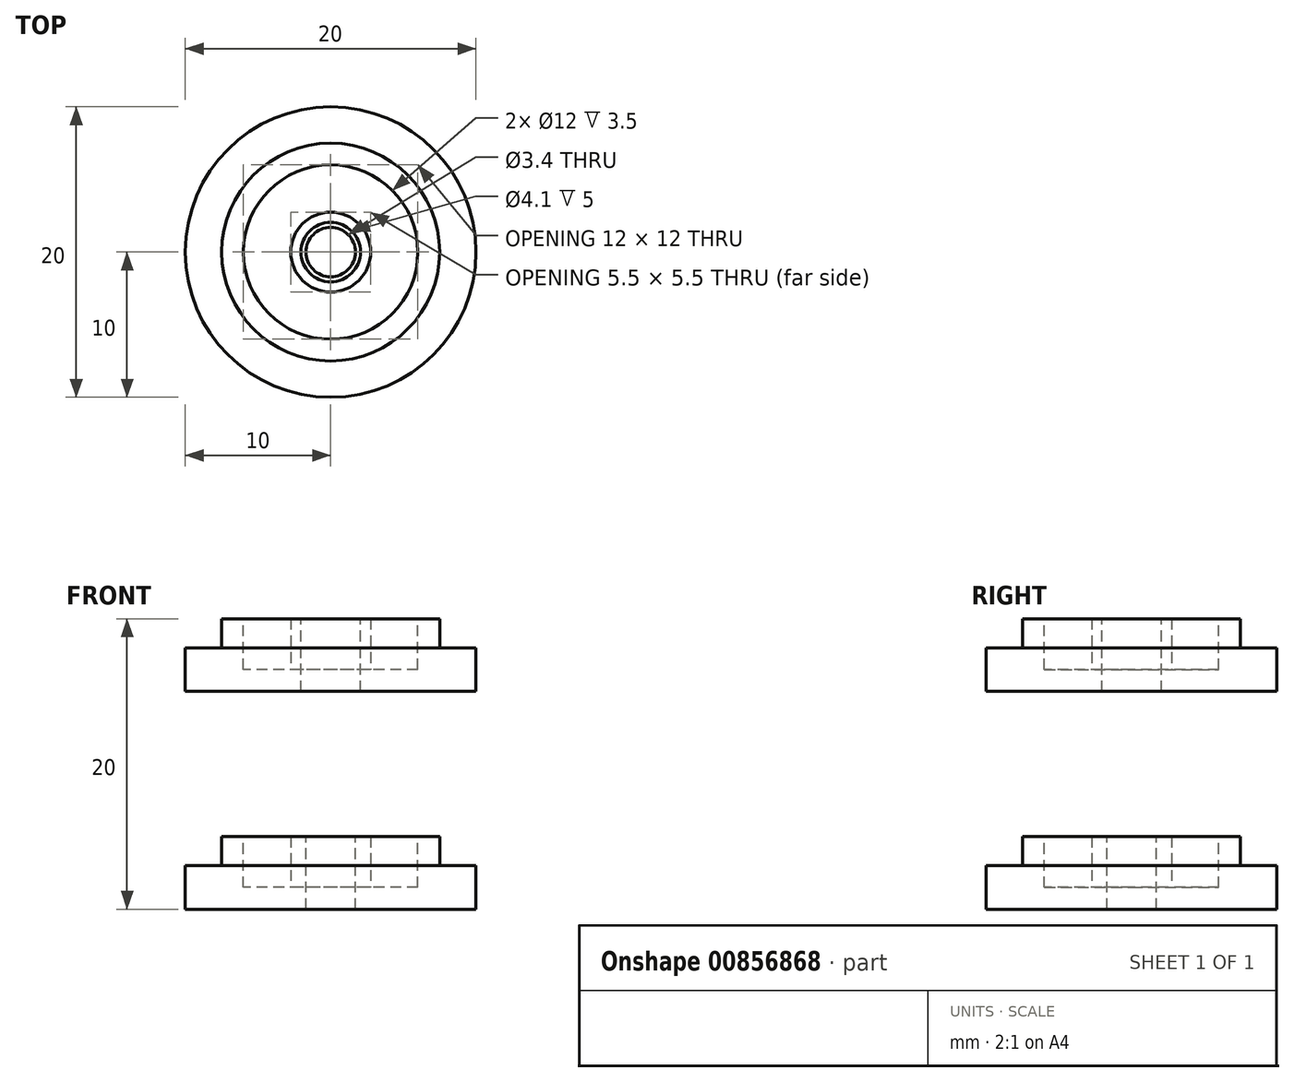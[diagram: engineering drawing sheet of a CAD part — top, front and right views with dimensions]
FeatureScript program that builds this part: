
annotation { "Feature Type Name" : "Feature", "Feature Type Description" : "" }
export const myFeature = defineFeature(function(context is Context, id is Id, definition is map)
    precondition{}
    {
        {
            var Q0;
            Q0=qCreatedBy(makeId("Right.planeOp"),FACE);
            var sketch = newSketch(context, id + "F0", { "sketchPlane" : qUnion([Q0])});
            skLineSegment(sketch, "E0", {"start": v(-7.5, 0) * mm, "end": v(-7.5, 2) * mm});
            skLineSegment(sketch, "E1", {"start": v(-7.5, 2) * mm, "end": v(0, 2) * mm});
            skLineSegment(sketch, "E2", {"start": v(0, 2) * mm, "end": v(0, 0) * mm});
            skLineSegment(sketch, "E3", {"start": v(0, 0) * mm, "end": v(-7.5, 0) * mm});
            skLineSegment(sketch, "E4.bottom", {"start": v(0, 0) * mm, "end": v(-10, 0) * mm});
            skLineSegment(sketch, "E4.top", {"start": v(0, -3) * mm, "end": v(-10, -3) * mm});
            skLineSegment(sketch, "E4.left", {"start": v(0, 0) * mm, "end": v(0, -3) * mm});
            skLineSegment(sketch, "E4.right", {"start": v(-10, 0) * mm, "end": v(-10, -3) * mm});
            skSolve(sketch);
        }
        {
            var Q0;
            Q0=makeQuery(id+"F0.imprint","IMPRINT",FACE,{"disambiguationData":[TD([[makeQuery(id+"F0.imprint","IMPRINT",EDGE,{"derivedFrom":sQuery(id+"F0.wireOp",EDGE,"E0")}),-1.0]])]});
            var Q1;
            Q1=makeQuery(id+"F0.imprint","IMPRINT",FACE,{"disambiguationData":[TD([[makeQuery(id+"F0.imprint","IMPRINT",EDGE,{"derivedFrom":sQuery(id+"F0.wireOp",EDGE,"E3")}),1.0]])]});
            var Q2;
            Q2=sQuery(id+"F0.wireOp",EDGE,"E2");
            revolve(context, id + "F1", {"surfaceOperationType" : NewSurfaceOperationType.NEW, "entities" : qUnion([Q0, Q1]), "axis" : qUnion([Q2]), "revolveType" : RevolveType.FULL});
        }
        {
            var Q0;
            Q0=makeQuery(id+"F1.opRevolve","SWEPT_FACE",FACE,{"disambiguationData":[OSD([sQuery(id+"F0.wireOp",EDGE,"E1")])]});
            shell(context, id + "F2", {"entities" : qUnion([Q0]), "thickness" : 1.5 * mm});
        }
        {
            var Q0;
            Q0=makeQuery(id+"F2.opShell","OFFSET_FACE",FACE,{"disambiguationData":[OSD([sQuery(id+"F0.wireOp",EDGE,"E4.top")])]});
            var sketch = newSketch(context, id + "F3", { "sketchPlane" : qUnion([Q0])});
            skCircle(sketch, "E5", {"center": v(0, 0) * mm, "radius": 2.75 * mm});
            skSolve(sketch);
        }
        {
            var Q0;
            Q0=makeQuery(id+"F3.imprint","IMPRINT",FACE,{"disambiguationData":[TD([[makeQuery(id+"F3.imprint","IMPRINT",EDGE,{"derivedFrom":sQuery(id+"F3.wireOp",EDGE,"E5")}),1.0]])]});
            var Q1;
            Q1=makeQuery(id+"F1.opRevolve","SWEPT_FACE",FACE,{"disambiguationData":[OSD([sQuery(id+"F0.wireOp",EDGE,"E1")])]});
            extrude(context, id + "F4", {"entities" : qUnion([Q0]), "operationType" : NewBodyOperationType.ADD, "endBound" : BoundingType.UP_TO_SURFACE, "depth" : 25 * mm, "endBoundEntityFace" : qUnion([Q1]), "offsetDistance" : 25 * mm});
        }
        {
            var Q0;
            Q0=makeQuery(id+"F4.opExtrude","CAP_FACE",FACE,{"disambiguationData":[OSD([sQuery(id+"F3.wireOp",EDGE,"E5")])],"isStart":false});
            var sketch = newSketch(context, id + "F5", { "sketchPlane" : qUnion([Q0])});
            skCircle(sketch, "E6", {"center": v(0, 0) * mm, "radius": 1.7 * mm});
            skSolve(sketch);
        }
        {
            var Q0;
            Q0=makeQuery(id+"F1.opRevolve","SWEPT_BODY",BODY,{"disambiguationData":[OSD([sQuery(id+"F0.wireOp",EDGE,"E0"),sQuery(id+"F0.wireOp",EDGE,"E1"),sQuery(id+"F0.wireOp",EDGE,"E2"),sQuery(id+"F0.wireOp",EDGE,"E4.bottom"),sQuery(id+"F0.wireOp",EDGE,"E4.top"),sQuery(id+"F0.wireOp",EDGE,"E4.left"),sQuery(id+"F0.wireOp",EDGE,"E4.right")])]});
            transform(context, id + "F6", {"entities" : qUnion([Q0]), "transformType" : TransformType.TRANSLATION_3D, "dx" : 0 * mm, "dy" : 0 * mm, "dz" : 15 * mm, "makeCopy" : true});
        }
        {
            var Q0;
            Q0=makeQuery(id+"F6.opPattern","COPY",FACE,{"derivedFrom":makeQuery(id+"F4.opExtrude","CAP_FACE",FACE,{"disambiguationData":[OSD([sQuery(id+"F3.wireOp",EDGE,"E5")])],"isStart":false}),"instanceName":"1"});
            var sketch = newSketch(context, id + "F7", { "sketchPlane" : qUnion([Q0])});
            skCircle(sketch, "E7", {"center": v(0, 0) * mm, "radius": 2.05 * mm});
            skSolve(sketch);
        }
        {
            var Q0;
            Q0=makeQuery(id+"F5.imprint","IMPRINT",FACE,{"disambiguationData":[TD([[makeQuery(id+"F5.imprint","IMPRINT",EDGE,{"derivedFrom":sQuery(id+"F5.wireOp",EDGE,"E6")}),1.0]])]});
            var Q1;
            Q1=makeQuery(id+"F1.opRevolve","SWEPT_FACE",FACE,{"disambiguationData":[OSD([sQuery(id+"F0.wireOp",EDGE,"E4.top")])]});
            extrude(context, id + "F8", {"entities" : qUnion([Q0]), "operationType" : NewBodyOperationType.REMOVE, "endBound" : BoundingType.UP_TO_SURFACE, "oppositeDirection" : true, "depth" : 25 * mm, "endBoundEntityFace" : qUnion([Q1]), "offsetDistance" : 25 * mm});
        }
        {
            var Q0;
            Q0=makeQuery(id+"F7.imprint","IMPRINT",FACE,{"disambiguationData":[TD([[makeQuery(id+"F7.imprint","IMPRINT",EDGE,{"derivedFrom":sQuery(id+"F7.wireOp",EDGE,"E7")}),1.0]])]});
            var Q1;
            Q1=makeQuery(id+"F6.opPattern","COPY",FACE,{"derivedFrom":makeQuery(id+"F1.opRevolve","SWEPT_FACE",FACE,{"disambiguationData":[OSD([sQuery(id+"F0.wireOp",EDGE,"E4.top")])]}),"instanceName":"1"});
            extrude(context, id + "F9", {"entities" : qUnion([Q0]), "operationType" : NewBodyOperationType.REMOVE, "endBound" : BoundingType.UP_TO_SURFACE, "oppositeDirection" : true, "depth" : 25 * mm, "endBoundEntityFace" : qUnion([Q1]), "offsetDistance" : 25 * mm});
        }
    });
